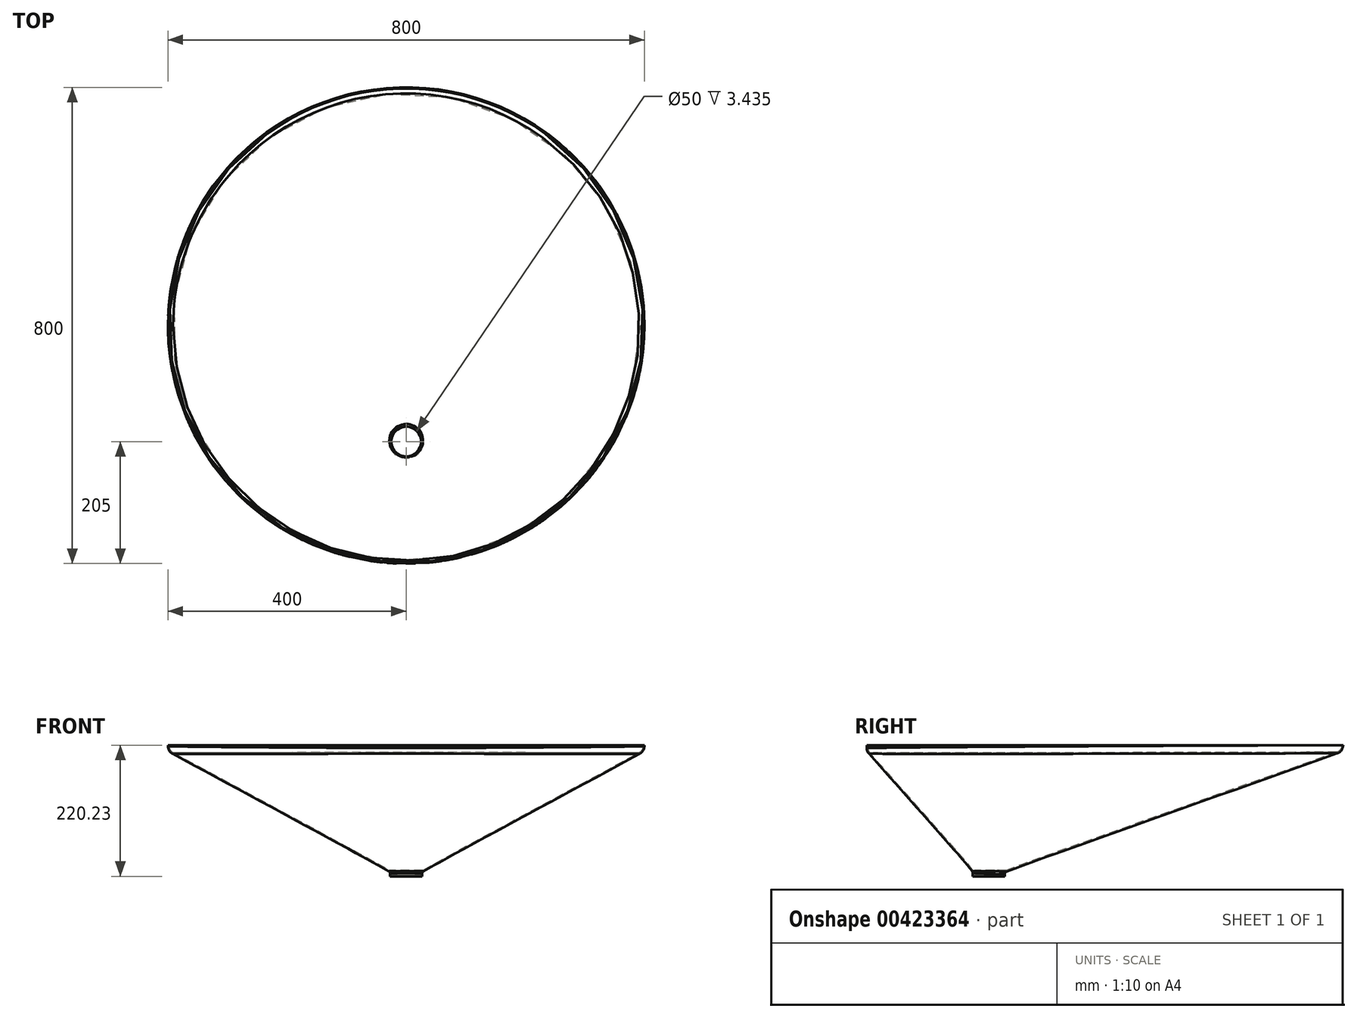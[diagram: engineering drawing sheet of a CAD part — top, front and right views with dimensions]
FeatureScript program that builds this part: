
annotation { "Feature Type Name" : "Feature", "Feature Type Description" : "" }
export const myFeature = defineFeature(function(context is Context, id is Id, definition is map)
    precondition{}
    {
        {
            var Q0;
            Q0=qCreatedBy(makeId("Top.planeOp"),FACE);
            var sketch = newSketch(context, id + "F0", { "sketchPlane" : qUnion([Q0])});
            skCircle(sketch, "E0", {"center": v(0, 0) * mm, "radius": 27 * mm});
            skSolve(sketch);
        }
        {
            var Q0;
            Q0=qCreatedBy(makeId("Top.planeOp"),FACE);
            cPlane(context, id + "F1", {"entities" : qUnion([Q0]), "cplaneType" : CPlaneType.OFFSET, "offset" : 203 * mm, "width" : 150 * mm, "height" : 150 * mm});
        }
        {
            var Q0;
            Q0=qCreatedBy(id+"F1.planeOp",FACE);
            var sketch = newSketch(context, id + "F2", { "sketchPlane" : qUnion([Q0])});
            skCircle(sketch, "E1", {"center": v(0, 195) * mm, "radius": 400 * mm});
            skSolve(sketch);
        }
        {
            var Q0;
            Q0=makeQuery(id+"F2.imprint","IMPRINT",FACE,{"disambiguationData":[TD([[makeQuery(id+"F2.imprint","IMPRINT",EDGE,{"derivedFrom":sQuery(id+"F2.wireOp",EDGE,"E1")}),1.0]])]});
            var Q1;
            Q1=makeQuery(id+"F0.imprint","IMPRINT",FACE,{"disambiguationData":[TD([[makeQuery(id+"F0.imprint","IMPRINT",EDGE,{"derivedFrom":sQuery(id+"F0.wireOp",EDGE,"E0")}),1.0]])]});
            loft(context, id + "F3", {"sheetProfilesArray" : [{ "sheetProfileEntities" : qUnion([Q0]) }, { "sheetProfileEntities" : qUnion([Q1]) }]});
        }
        {
            var Q0;
            Q0=makeQuery(id+"F3.opLoft","CAP_FACE",FACE,{"disambiguationData":[OSD([makeQuery(id+"F2.imprint","IMPRINT",FACE,{"disambiguationData":[TD([[makeQuery(id+"F2.imprint","IMPRINT",EDGE,{"derivedFrom":sQuery(id+"F2.wireOp",EDGE,"E1")}),1.0]])]})])],"isStart":true});
            extrude(context, id + "F4", {"entities" : qUnion([Q0]), "operationType" : NewBodyOperationType.ADD, "depth" : 10 * mm});
        }
        {
            var Q0;
            Q0=makeQuery(id+"F3.opLoft","CAP_FACE",FACE,{"disambiguationData":[OSD([makeQuery(id+"F0.imprint","IMPRINT",FACE,{"disambiguationData":[TD([[makeQuery(id+"F0.imprint","IMPRINT",EDGE,{"derivedFrom":sQuery(id+"F0.wireOp",EDGE,"E0")}),1.0]])]})])],"isStart":true});
            extrude(context, id + "F5", {"entities" : qUnion([Q0]), "operationType" : NewBodyOperationType.ADD, "depth" : 7 * mm});
        }
        {
            var Q0;
            {var subQ0=sQuery(id+"F2.wireOp",EDGE,"E1");Q0=makeQuery(id+"F4.boolean.opBoolean","MERGE",EDGE,{"derivedFrom":[makeQuery(id+"F3.opLoft","MID_CAP_EDGE",EDGE,{"disambiguationData":[OSD([subQ0])],"capPos":0.0}),makeQuery(id+"F4.opExtrude","CAP_EDGE",EDGE,{"disambiguationData":[OSD([subQ0])],"isStart":true})]});}
            fillet(context, id + "F6", {"entities" : qUnion([Q0]), "radius" : 14.5 * mm, "tangentPropagation" : true, "allowEdgeOverflow" : false});
        }
        {
            var Q0;
            {var subQ0=sQuery(id+"F2.wireOp",EDGE,"E1");var subQ1=sQuery(id+"F0.wireOp",EDGE,"E0");Q0=makeQuery(id+"F5.boolean.opBoolean","MERGE",EDGE,{"derivedFrom":[makeQuery(id+"F3.opLoft","MID_CAP_EDGE",EDGE,{"disambiguationData":[OSD([subQ1,subQ0])],"capPos":1.0}),makeQuery(id+"F5.opExtrude","CAP_EDGE",EDGE,{"disambiguationData":[OSD([subQ1,subQ0])],"isStart":true})]});}
            fillet(context, id + "F7", {"entities" : qUnion([Q0]), "radius" : 5 * mm, "tangentPropagation" : true, "allowEdgeOverflow" : false});
        }
        {
            var Q0;
            Q0=makeQuery(id+"F4.opExtrude","CAP_FACE",FACE,{"disambiguationData":[OSD([makeQuery(id+"F2.imprint","IMPRINT",FACE,{"disambiguationData":[TD([[makeQuery(id+"F2.imprint","IMPRINT",EDGE,{"derivedFrom":sQuery(id+"F2.wireOp",EDGE,"E1")}),1.0]])]})])],"isStart":false});
            shell(context, id + "F8", {"entities" : qUnion([Q0]), "thickness" : 2 * mm});
        }
    });
